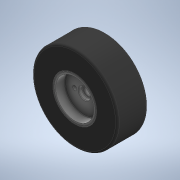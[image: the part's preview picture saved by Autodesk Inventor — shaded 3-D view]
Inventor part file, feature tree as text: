
AUTODESK INVENTOR PART (.ipt)
format: ipt  version: 2022 (Build 260153000, 153)  size: 370,176 bytes
history: native  units: in
note: dims shown in document units (in); Inventor stores cm internally (conversion verified against a paired STEP export)
features: fillet x3, sketch x3, extrude x2, revolve x1
ambient origin geometry x8: Origin, YZ Plane, XZ Plane, XY Plane, X Axis, Y Axis, Z Axis, Center Point
bodies: Solid1 (feature_tree)
feature tree (9):
  revolve  "Revolution1"  [1 undecoded]
  fillet  "Fillet1"  Radius=0.6875in
  fillet  "Fillet2"  Radius=0.0625in
  extrude  "Extrusion1"  Depth=0.125in
  extrude  "Extrusion2"  Depth=0.1875in
  fillet  "Fillet3"  Radius=0.3125in
  sketch  "Sketch1"  dims[d0=1.4in d1=1.0in d2=0.6875in d3=0.0625in]
  sketch  "Sketch2"  dims[d4=0.3125in d5=0.5625in d6=0.125in]
  sketch  "Sketch3"  dims[d7=0.275in d9=0.1875in d10=0.3125in d11=0.125in d12=360.0deg d13=0.0197in d14=0.0039in d15=0.0197in d16=0.0039in d17=0.0312in d18=0.0625in d19=0.625in d20=0.325in d21=0.64in d22=0.15in d23=0.25in d24=0.7874in d26=360.0deg d28=1.0in d29=0.0in d30=0.625in d31=0.138in d32=0.7874in d34=360.0deg d36=0.0in d37=0.0in d38=0.0197in]
note: 1 required parameter value undecoded (feature->parameter linkage not recoverable at this tier; creation-order binding heuristic only, values carry confidence <= 0.55)
